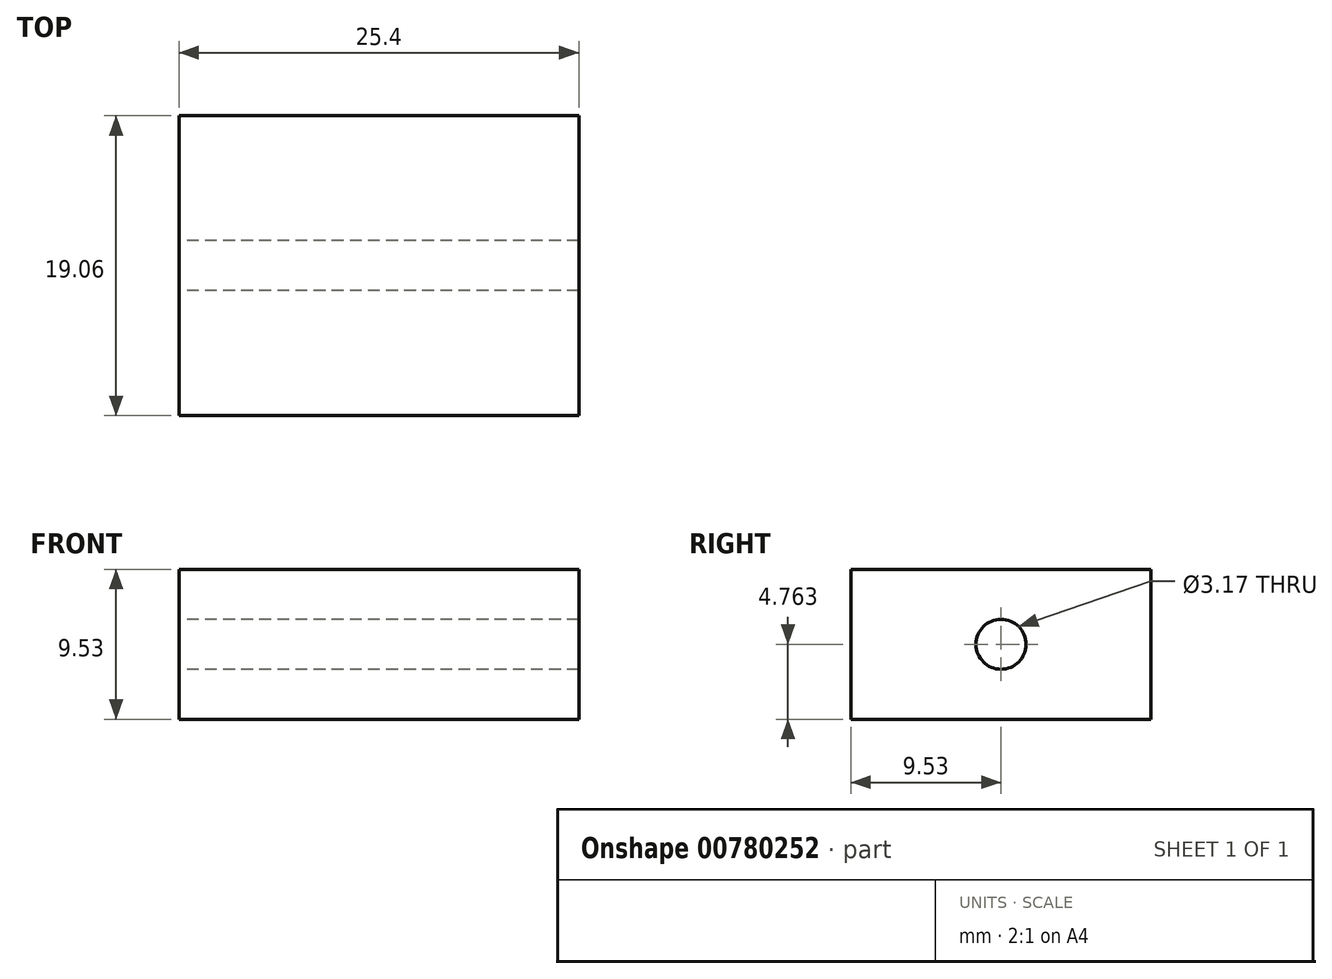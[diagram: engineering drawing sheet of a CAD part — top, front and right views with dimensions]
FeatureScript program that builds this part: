
annotation { "Feature Type Name" : "Feature", "Feature Type Description" : "" }
export const myFeature = defineFeature(function(context is Context, id is Id, definition is map)
    precondition{}
    {
        {
            var Q0;
            Q0=qCreatedBy(makeId("Top.planeOp"),FACE);
            var sketch = newSketch(context, id + "F0", { "sketchPlane" : qUnion([Q0])});
            skLineSegment(sketch, "E0.bottom", {"start": v(12.7, -9.53) * mm, "end": v(-12.7, -9.53) * mm});
            skLineSegment(sketch, "E0.top", {"start": v(12.7, 9.53) * mm, "end": v(-12.7, 9.52) * mm});
            skLineSegment(sketch, "E0.left", {"start": v(12.7, -9.52) * mm, "end": v(12.7, 9.53) * mm});
            skLineSegment(sketch, "E0.right", {"start": v(-12.7, -9.53) * mm, "end": v(-12.7, 9.52) * mm});
            skPoint(sketch, "E0.middle", {"position": v(0, 0) * mm});
            skSolve(sketch);
        }
        {
            var Q0;
            Q0=makeQuery(id+"F0.imprint","IMPRINT",FACE,{"disambiguationData":[TD([[makeQuery(id+"F0.imprint","IMPRINT",EDGE,{"derivedFrom":sQuery(id+"F0.wireOp",EDGE,"E0.bottom")}),-1.0]])]});
            extrude(context, id + "F1", {"entities" : qUnion([Q0]), "depth" : 9.52 * mm, "offsetDistance" : 25.4 * mm});
        }
        {
            var Q0;
            Q0=makeQuery(id+"F1.opExtrude","SWEPT_FACE",FACE,{"disambiguationData":[OSD([sQuery(id+"F0.wireOp",EDGE,"E0.right")])]});
            var sketch = newSketch(context, id + "F2", { "sketchPlane" : qUnion([Q0])});
            skCircle(sketch, "E1", {"center": v(0, 4.76) * mm, "radius": 1.59 * mm});
            skSolve(sketch);
        }
        {
            var Q0;
            Q0=makeQuery(id+"F2.imprint","IMPRINT",FACE,{"disambiguationData":[TD([[makeQuery(id+"F2.imprint","IMPRINT",EDGE,{"derivedFrom":sQuery(id+"F2.wireOp",EDGE,"E1")}),1.0]])]});
            extrude(context, id + "F3", {"entities" : qUnion([Q0]), "operationType" : NewBodyOperationType.REMOVE, "oppositeDirection" : true, "depth" : 25.4 * mm, "offsetDistance" : 25.4 * mm});
        }
    });
